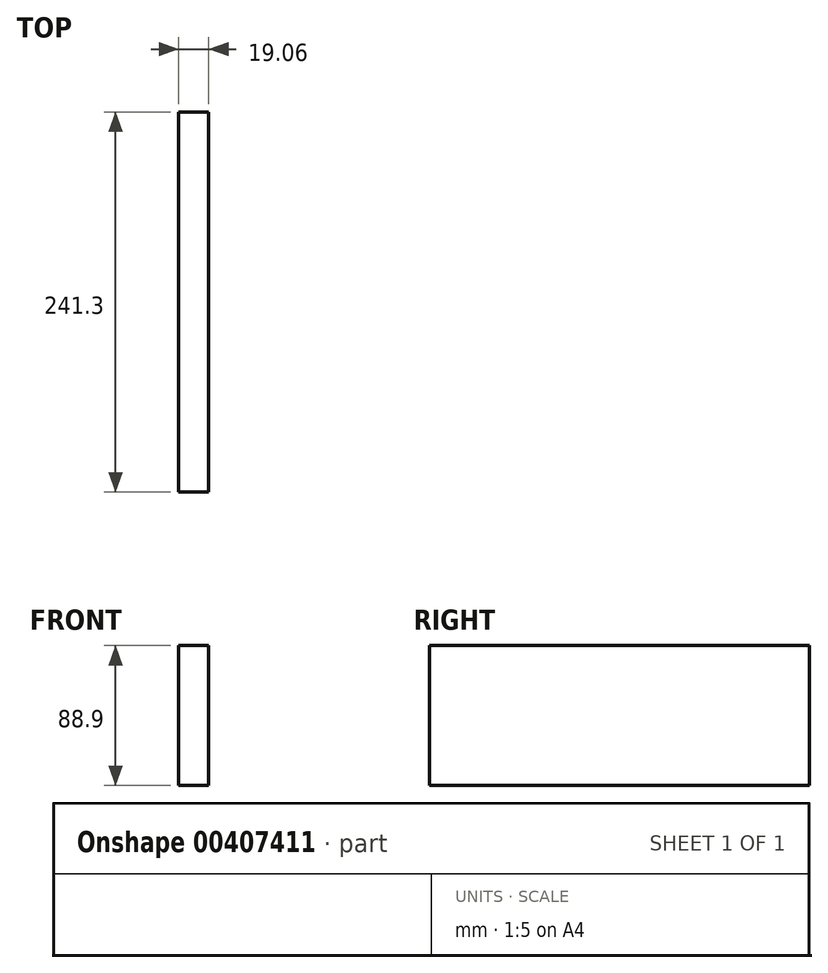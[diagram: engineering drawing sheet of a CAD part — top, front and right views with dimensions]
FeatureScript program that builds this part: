
annotation { "Feature Type Name" : "Feature", "Feature Type Description" : "" }
export const myFeature = defineFeature(function(context is Context, id is Id, definition is map)
    precondition{}
    {
        {
            var Q0;
            Q0=qCreatedBy(makeId("Front.planeOp"),FACE);
            var sketch = newSketch(context, id + "F0", { "sketchPlane" : qUnion([Q0])});
            skLineSegment(sketch, "E0.bottom", {"start": v(9.53, 44.45) * mm, "end": v(-9.52, 44.45) * mm});
            skLineSegment(sketch, "E0.top", {"start": v(9.52, -44.45) * mm, "end": v(-9.53, -44.45) * mm});
            skLineSegment(sketch, "E0.left", {"start": v(9.53, 44.45) * mm, "end": v(9.52, -44.45) * mm});
            skLineSegment(sketch, "E0.right", {"start": v(-9.52, 44.45) * mm, "end": v(-9.53, -44.45) * mm});
            skPoint(sketch, "E0.middle", {"position": v(0, 0) * mm});
            skSolve(sketch);
        }
        {
            var Q0;
            Q0=makeQuery(id+"F0.imprint","IMPRINT",FACE,{"disambiguationData":[TD([[makeQuery(id+"F0.imprint","IMPRINT",EDGE,{"derivedFrom":sQuery(id+"F0.wireOp",EDGE,"E0.bottom")}),1.0]])]});
            extrude(context, id + "F1", {"entities" : qUnion([Q0]), "depth" : 241.3 * mm});
        }
    });
